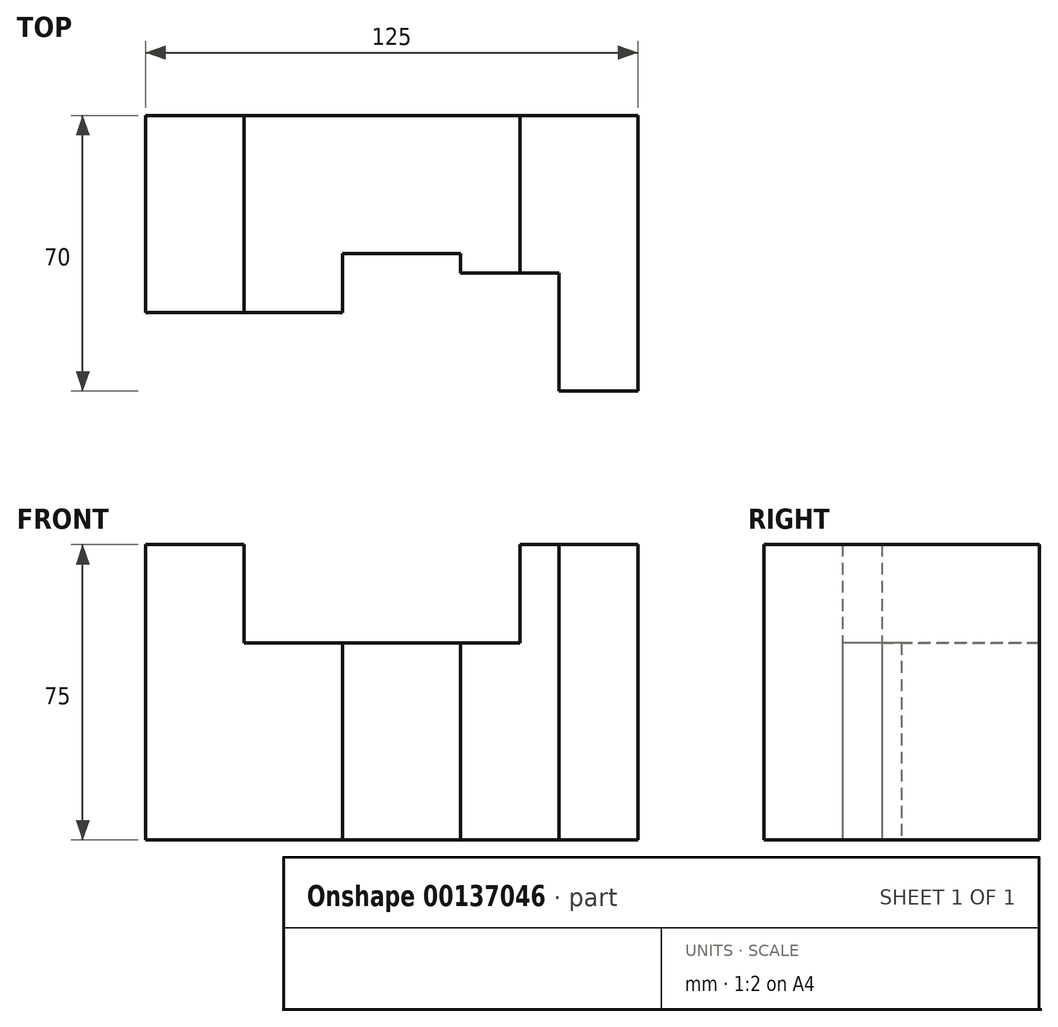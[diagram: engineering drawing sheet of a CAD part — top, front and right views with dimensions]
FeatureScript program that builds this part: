
annotation { "Feature Type Name" : "Feature", "Feature Type Description" : "" }
export const myFeature = defineFeature(function(context is Context, id is Id, definition is map)
    precondition{}
    {
        {
            var Q0;
            Q0=qCreatedBy(makeId("Top.planeOp"),FACE);
            var sketch = newSketch(context, id + "F0", { "sketchPlane" : qUnion([Q0])});
            skLineSegment(sketch, "E0", {"start": v(0, 0) * mm, "end": v(0, 50) * mm});
            skLineSegment(sketch, "E1", {"start": v(0, 50) * mm, "end": v(25, 50) * mm});
            skLineSegment(sketch, "E2", {"start": v(25, 50) * mm, "end": v(25, 0) * mm});
            skLineSegment(sketch, "E3", {"start": v(25, 0) * mm, "end": v(0, 0) * mm});
            skLineSegment(sketch, "E4", {"start": v(25, 50) * mm, "end": v(95, 50) * mm});
            skLineSegment(sketch, "E5", {"start": v(80, 15) * mm, "end": v(50, 15) * mm});
            skLineSegment(sketch, "E6", {"start": v(50, 15) * mm, "end": v(50, 0) * mm});
            skLineSegment(sketch, "E7", {"start": v(50, 0) * mm, "end": v(25, 0) * mm});
            skLineSegment(sketch, "E8", {"start": v(105, -20) * mm, "end": v(125, -20) * mm});
            skLineSegment(sketch, "E9", {"start": v(125, -20) * mm, "end": v(125, 50) * mm});
            skLineSegment(sketch, "E10", {"start": v(125, 50) * mm, "end": v(95, 50) * mm});
            skLineSegment(sketch, "E11", {"start": v(80, 15) * mm, "end": v(80, 10) * mm});
            skLineSegment(sketch, "E12", {"start": v(80, 10) * mm, "end": v(95, 10) * mm});
            skLineSegment(sketch, "E13", {"start": v(95, 10) * mm, "end": v(95, 50) * mm});
            skLineSegment(sketch, "E14", {"start": v(95, 10) * mm, "end": v(105, 10) * mm});
            skLineSegment(sketch, "E15", {"start": v(105, 10) * mm, "end": v(105, -20) * mm});
            skSolve(sketch);
        }
        {
            var Q0;
            Q0=makeQuery(id+"F0.imprint","IMPRINT",FACE,{"disambiguationData":[TD([[makeQuery(id+"F0.imprint","IMPRINT",EDGE,{"derivedFrom":sQuery(id+"F0.wireOp",EDGE,"E0")}),-1.0]])]});
            var Q1;
            Q1=makeQuery(id+"F0.imprint","IMPRINT",FACE,{"disambiguationData":[TD([[makeQuery(id+"F0.imprint","IMPRINT",EDGE,{"derivedFrom":sQuery(id+"F0.wireOp",EDGE,"E8")}),1.0]])]});
            extrude(context, id + "F1", {"entities" : qUnion([Q0, Q1]), "depth" : 75 * mm});
        }
        {
            var Q0;
            Q0=makeQuery(id+"F0.imprint","IMPRINT",FACE,{"disambiguationData":[TD([[makeQuery(id+"F0.imprint","IMPRINT",EDGE,{"derivedFrom":sQuery(id+"F0.wireOp",EDGE,"E2")}),1.0]])]});
            extrude(context, id + "F2", {"entities" : qUnion([Q0]), "operationType" : NewBodyOperationType.ADD, "depth" : 50 * mm});
        }
    });
